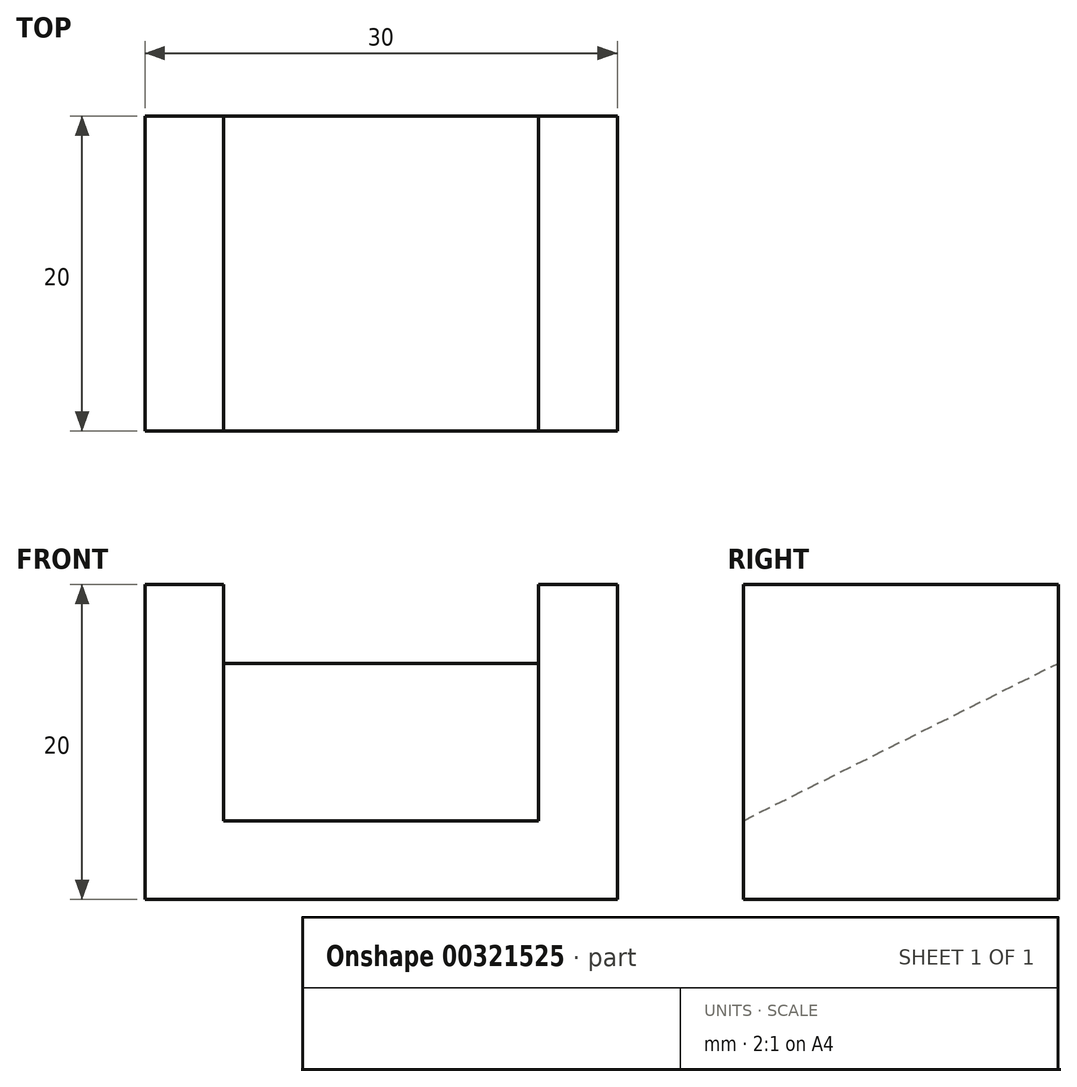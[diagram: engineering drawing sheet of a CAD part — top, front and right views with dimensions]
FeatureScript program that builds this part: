
annotation { "Feature Type Name" : "Feature", "Feature Type Description" : "" }
export const myFeature = defineFeature(function(context is Context, id is Id, definition is map)
    precondition{}
    {
        {
            var Q0;
            Q0=qCreatedBy(makeId("Front.planeOp"),FACE);
            var sketch = newSketch(context, id + "F0", { "sketchPlane" : qUnion([Q0])});
            skLineSegment(sketch, "E0", {"start": v(-15, 20) * mm, "end": v(-15, 0) * mm});
            skLineSegment(sketch, "E1", {"start": v(-15, 0) * mm, "end": v(15, 0) * mm});
            skLineSegment(sketch, "E2", {"start": v(15, 0) * mm, "end": v(15, 20) * mm});
            skLineSegment(sketch, "E3", {"start": v(15, 20) * mm, "end": v(10, 20) * mm});
            skLineSegment(sketch, "E4", {"start": v(10, 20) * mm, "end": v(10, 5) * mm});
            skLineSegment(sketch, "E5", {"start": v(10, 5) * mm, "end": v(-10, 5) * mm});
            skLineSegment(sketch, "E6", {"start": v(-10, 5) * mm, "end": v(-10, 20) * mm});
            skLineSegment(sketch, "E7", {"start": v(-10, 20) * mm, "end": v(-15, 20) * mm});
            skSolve(sketch);
        }
        {
            var Q0;
            Q0 = qSketchRegion(id + "F0", true);
            extrude(context, id + "F1", {"entities" : qUnion([Q0]), "depth" : 20 * mm});
        }
        {
            var Q0;
            Q0=qCreatedBy(makeId("Right.planeOp"),FACE);
            var sketch = newSketch(context, id + "F2", { "sketchPlane" : qUnion([Q0])});
            skLineSegment(sketch, "E8", {"start": v(0, 5) * mm, "end": v(0, 15) * mm});
            skLineSegment(sketch, "E9", {"start": v(0, 15) * mm, "end": v(-20, 5) * mm});
            skLineSegment(sketch, "E10", {"start": v(-20, 5) * mm, "end": v(0, 5) * mm});
            skSolve(sketch);
        }
        {
            var Q0;
            Q0 = qSketchRegion(id + "F2", true);
            var Q1;
            Q1=makeQuery(id+"F1.opExtrude","SWEPT_FACE",FACE,{"disambiguationData":[OSD([sQuery(id+"F0.wireOp",EDGE,"E6")])]});
            var Q2;
            Q2=makeQuery(id+"F1.opExtrude","SWEPT_FACE",FACE,{"disambiguationData":[OSD([sQuery(id+"F0.wireOp",EDGE,"E4")])]});
            extrude(context, id + "F3", {"entities" : qUnion([Q0]), "operationType" : NewBodyOperationType.ADD, "endBound" : BoundingType.UP_TO_SURFACE, "oppositeDirection" : true, "endBoundEntityFace" : qUnion([Q1]), "depth" : 25 * mm, "hasSecondDirection" : true, "secondDirectionBound" : SecondDirectionBoundingType.UP_TO_SURFACE, "secondDirectionOppositeDirection" : false, "secondDirectionBoundEntityFace" : qUnion([Q2]), "secondDirectionDepth" : 25 * mm});
        }
    });
